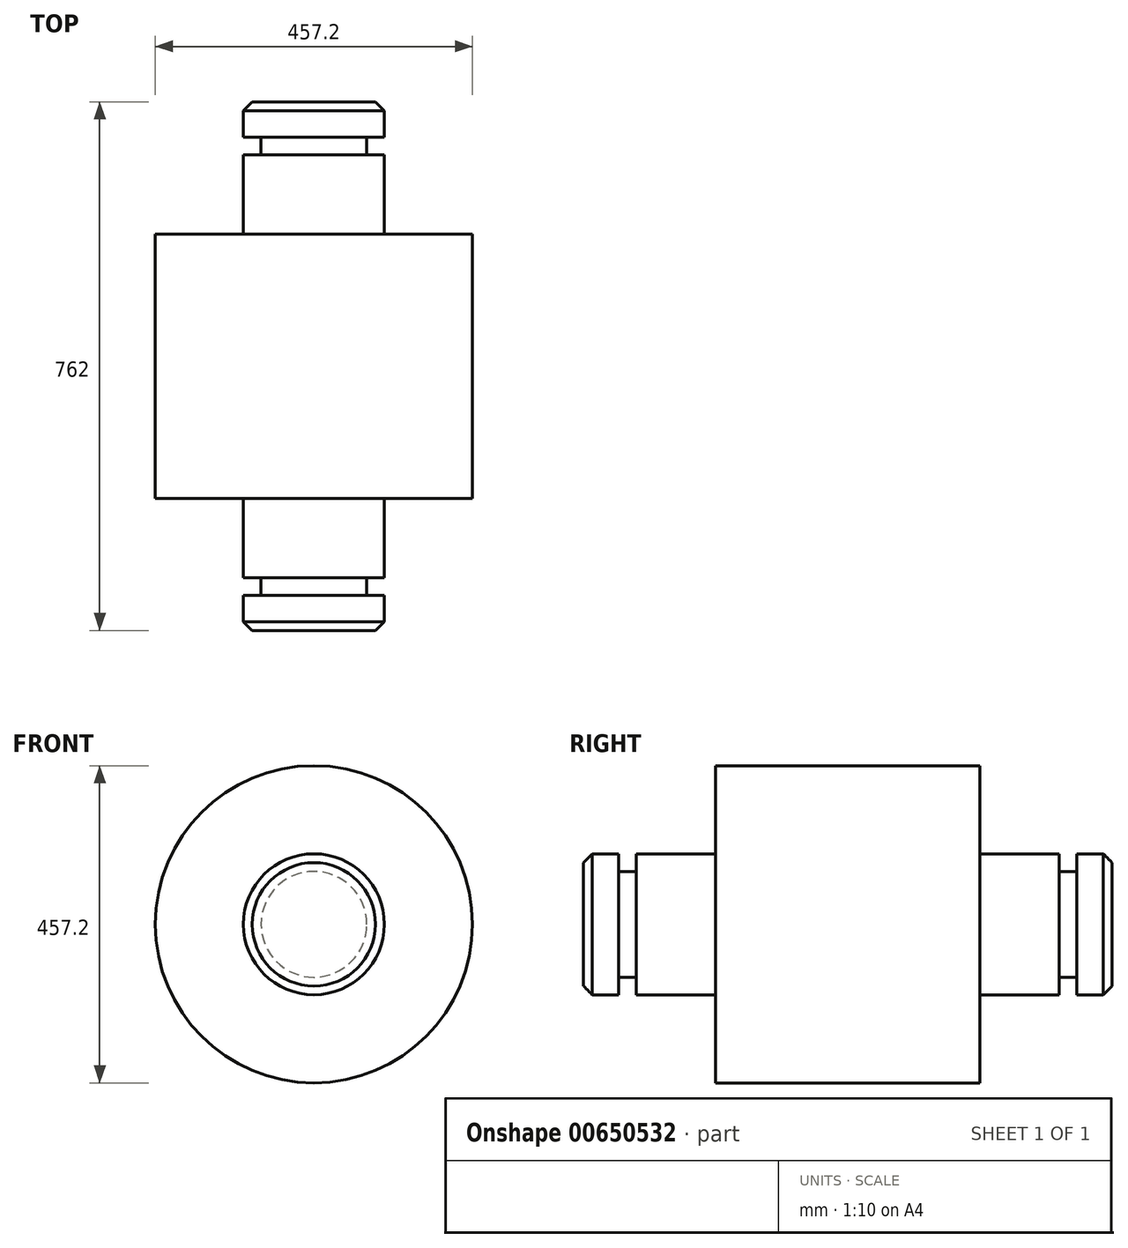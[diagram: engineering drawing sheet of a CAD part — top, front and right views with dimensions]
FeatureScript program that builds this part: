
annotation { "Feature Type Name" : "Feature", "Feature Type Description" : "" }
export const myFeature = defineFeature(function(context is Context, id is Id, definition is map)
    precondition{}
    {
        {
            var Q0;
            Q0=qCreatedBy(makeId("Front.planeOp"),FACE);
            var sketch = newSketch(context, id + "F0", { "sketchPlane" : qUnion([Q0])});
            skCircle(sketch, "E0", {"center": v(0, 0) * mm, "radius": 228.6 * mm});
            skSolve(sketch);
        }
        {
            var Q0;
            Q0 = qSketchRegion(id + "F0", true);
            extrude(context, id + "F1", {"entities" : qUnion([Q0]), "depth" : 381 * mm, "offsetDistance" : 25.4 * mm});
        }
        {
            var Q0;
            Q0=makeQuery(id+"F1.opExtrude","CAP_FACE",FACE,{"disambiguationData":[OSD([sQuery(id+"F0.wireOp",EDGE,"E0")])],"isStart":false});
            var sketch = newSketch(context, id + "F2", { "sketchPlane" : qUnion([Q0])});
            skCircle(sketch, "E1", {"center": v(0, 0) * mm, "radius": 101.6 * mm});
            skSolve(sketch);
        }
        {
            var Q0;
            Q0 = qSketchRegion(id + "F2", true);
            extrude(context, id + "F3", {"entities" : qUnion([Q0]), "operationType" : NewBodyOperationType.ADD, "depth" : 114.3 * mm, "offsetDistance" : 25.4 * mm});
        }
        {
            var Q0;
            Q0=makeQuery(id+"F1.opExtrude","CAP_FACE",FACE,{"disambiguationData":[OSD([sQuery(id+"F0.wireOp",EDGE,"E0")])],"isStart":true});
            var sketch = newSketch(context, id + "F4", { "sketchPlane" : qUnion([Q0])});
            skCircle(sketch, "E2", {"center": v(0, 0) * mm, "radius": 101.6 * mm});
            skSolve(sketch);
        }
        {
            var Q0;
            Q0 = qSketchRegion(id + "F4", true);
            var Q1;
            Q1=makeQuery(id+"F3.opExtrude","CAP_FACE",FACE,{"disambiguationData":[OSD([sQuery(id+"F2.wireOp",EDGE,"E1")])],"isStart":false});
            extrude(context, id + "F5", {"entities" : qUnion([Q0, Q1]), "operationType" : NewBodyOperationType.ADD, "depth" : 114.3 * mm, "offsetDistance" : 25.4 * mm});
        }
        {
            var Q0;
            Q0=makeQuery(id+"F5.opExtrude","CAP_FACE",FACE,{"disambiguationData":[OSD([sQuery(id+"F4.wireOp",EDGE,"E2")])],"isStart":false});
            var sketch = newSketch(context, id + "F6", { "sketchPlane" : qUnion([Q0])});
            skCircle(sketch, "E3", {"center": v(0, 0) * mm, "radius": 76.2 * mm});
            skSolve(sketch);
        }
        {
            var Q0;
            Q0 = qSketchRegion(id + "F6", true);
            extrude(context, id + "F7", {"entities" : qUnion([Q0]), "operationType" : NewBodyOperationType.ADD, "depth" : 25.4 * mm, "offsetDistance" : 25.4 * mm});
        }
        {
            var Q0;
            Q0=makeQuery(id+"F7.opExtrude","CAP_FACE",FACE,{"disambiguationData":[OSD([sQuery(id+"F6.wireOp",EDGE,"E3")])],"isStart":false});
            var sketch = newSketch(context, id + "F8", { "sketchPlane" : qUnion([Q0])});
            skCircle(sketch, "E4", {"center": v(0, 0) * mm, "radius": 101.6 * mm});
            skSolve(sketch);
        }
        {
            var Q0;
            Q0 = qSketchRegion(id + "F8", true);
            extrude(context, id + "F9", {"entities" : qUnion([Q0]), "operationType" : NewBodyOperationType.ADD, "depth" : 50.8 * mm, "offsetDistance" : 25.4 * mm});
        }
        {
            var Q0;
            Q0=makeQuery(id+"F3.opExtrude","CAP_FACE",FACE,{"disambiguationData":[OSD([sQuery(id+"F2.wireOp",EDGE,"E1")])],"isStart":false});
            var sketch = newSketch(context, id + "F10", { "sketchPlane" : qUnion([Q0])});
            skCircle(sketch, "E5", {"center": v(0, 0) * mm, "radius": 76.2 * mm});
            skSolve(sketch);
        }
        {
            var Q0;
            Q0 = qSketchRegion(id + "F10", true);
            extrude(context, id + "F11", {"entities" : qUnion([Q0]), "operationType" : NewBodyOperationType.ADD, "depth" : 25.4 * mm, "offsetDistance" : 25.4 * mm});
        }
        {
            var Q0;
            Q0=makeQuery(id+"F11.opExtrude","CAP_FACE",FACE,{"disambiguationData":[OSD([sQuery(id+"F10.wireOp",EDGE,"E5")])],"isStart":false});
            var sketch = newSketch(context, id + "F12", { "sketchPlane" : qUnion([Q0])});
            skCircle(sketch, "E6", {"center": v(0, 0) * mm, "radius": 101.6 * mm});
            skSolve(sketch);
        }
        {
            var Q0;
            Q0 = qSketchRegion(id + "F12", true);
            extrude(context, id + "F13", {"entities" : qUnion([Q0]), "operationType" : NewBodyOperationType.ADD, "depth" : 50.8 * mm, "offsetDistance" : 25.4 * mm});
        }
        {
            var Q0;
            Q0=makeQuery(id+"F9.opExtrude","CAP_EDGE",EDGE,{"disambiguationData":[OSD([sQuery(id+"F8.wireOp",EDGE,"E4")])],"isStart":false});
            var Q1;
            Q1=makeQuery(id+"F13.opExtrude","CAP_EDGE",EDGE,{"disambiguationData":[OSD([sQuery(id+"F12.wireOp",EDGE,"E6")])],"isStart":false});
            chamfer(context, id + "F14", {"entities" : qUnion([Q0, Q1]), "chamferType" : ChamferType.OFFSET_ANGLE, "width" : 12.7 * mm, "oppositeDirection" : false, "angle" : 45 * degree});
        }
    });
